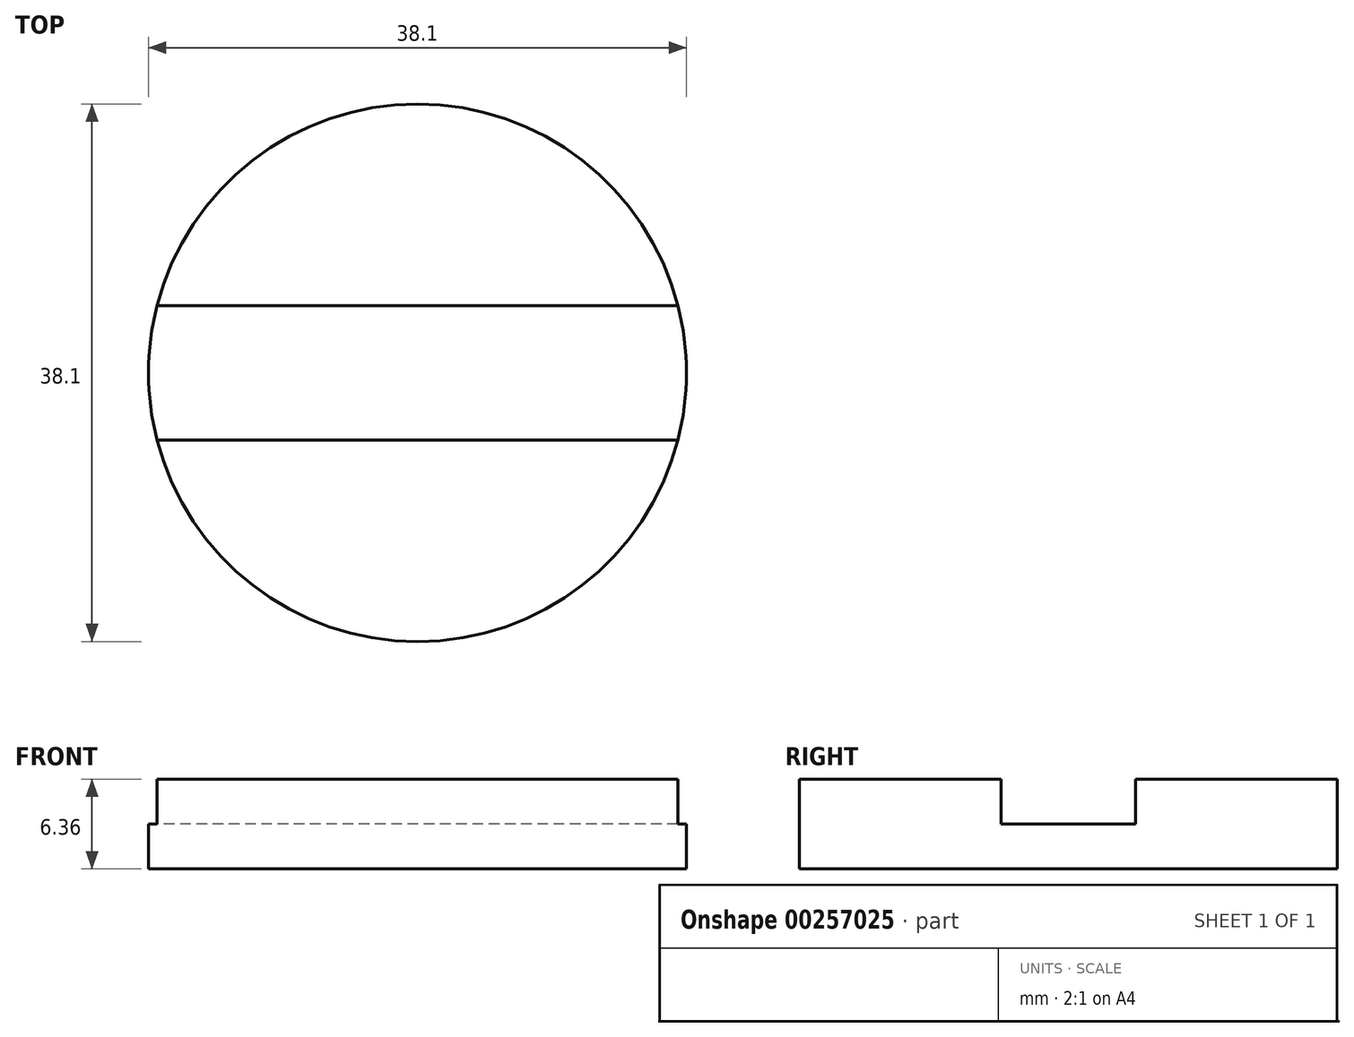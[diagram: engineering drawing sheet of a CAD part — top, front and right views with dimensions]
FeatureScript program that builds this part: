
annotation { "Feature Type Name" : "Feature", "Feature Type Description" : "" }
export const myFeature = defineFeature(function(context is Context, id is Id, definition is map)
    precondition{}
    {
        {
            var Q0;
            Q0=qCreatedBy(makeId("Top.planeOp"),FACE);
            var sketch = newSketch(context, id + "F0", { "sketchPlane" : qUnion([Q0])});
            skCircle(sketch, "E0", {"center": v(0, 0) * mm, "radius": 19.05 * mm});
            skLineSegment(sketch, "E1.bottom", {"start": v(18.45, 4.76) * mm, "end": v(-18.45, 4.76) * mm});
            skLineSegment(sketch, "E1.top", {"start": v(18.45, -4.76) * mm, "end": v(-18.45, -4.76) * mm});
            skLineSegment(sketch, "E1.left", {"start": v(18.45, 4.76) * mm, "end": v(18.45, -4.76) * mm});
            skLineSegment(sketch, "E1.right", {"start": v(-18.45, 4.76) * mm, "end": v(-18.45, -4.76) * mm});
            skLineSegment(sketch, "E2.bottom", {"start": v(25.4, 25.4) * mm, "end": v(-25.4, 25.4) * mm});
            skLineSegment(sketch, "E2.top", {"start": v(25.4, -25.4) * mm, "end": v(-25.4, -25.4) * mm});
            skLineSegment(sketch, "E2.left", {"start": v(25.4, 25.4) * mm, "end": v(25.4, -25.4) * mm});
            skLineSegment(sketch, "E2.right", {"start": v(-25.4, 25.4) * mm, "end": v(-25.4, -25.4) * mm});
            skLineSegment(sketch, "E3.bottom", {"start": v(-18.45, 4.76) * mm, "end": v(-25.4, 4.76) * mm});
            skLineSegment(sketch, "E3.top", {"start": v(-18.45, -4.76) * mm, "end": v(-25.4, -4.76) * mm});
            skLineSegment(sketch, "E3.right", {"start": v(-25.4, 4.76) * mm, "end": v(-25.4, -4.76) * mm});
            skLineSegment(sketch, "E4.bottom", {"start": v(-25.4, 4.76) * mm, "end": v(25.4, 4.76) * mm});
            skLineSegment(sketch, "E4.top", {"start": v(-25.4, -4.76) * mm, "end": v(25.4, -4.76) * mm});
            skLineSegment(sketch, "E4.right", {"start": v(25.4, 4.76) * mm, "end": v(25.4, -4.76) * mm});
            skSolve(sketch);
        }
        {
            var Q0;
            {var subQ0=sQuery(id+"F0.wireOp",EDGE,"E4.bottom");var subQ1=sQuery(id+"F0.wireOp",EDGE,"E0");var subQ2=makeQuery(id+"F0.imprint","INTERSECT",VERTEX,{"derivedFrom":[subQ1,sQuery(id+"F0.wireOp",EDGE,"E1.left"),subQ0]});Q0=makeQuery(id+"F0.imprint","IMPRINT",FACE,{"disambiguationData":[TD([[makeQuery(id+"F0.imprint","IMPRINT",EDGE,{"disambiguationData":[TD([[subQ2,-1.0]])],"derivedFrom":subQ1}),1.0]])]});}
            var Q1;
            {var subQ0=sQuery(id+"F0.wireOp",EDGE,"E4.top");var subQ1=sQuery(id+"F0.wireOp",EDGE,"E0");var subQ2=makeQuery(id+"F0.imprint","INTERSECT",VERTEX,{"derivedFrom":[subQ1,sQuery(id+"F0.wireOp",EDGE,"E1.left"),subQ0]});Q1=makeQuery(id+"F0.imprint","IMPRINT",FACE,{"disambiguationData":[TD([[makeQuery(id+"F0.imprint","IMPRINT",EDGE,{"disambiguationData":[TD([[subQ2,1.0]])],"derivedFrom":subQ1}),1.0]])]});}
            extrude(context, id + "F1", {"entities" : qUnion([Q0, Q1]), "depth" : 3.17 * mm});
        }
        {
            var Q0;
            {var subQ0=sQuery(id+"F0.wireOp",EDGE,"E4.bottom");var subQ1=sQuery(id+"F0.wireOp",EDGE,"E0");var subQ2=makeQuery(id+"F0.imprint","INTERSECT",VERTEX,{"derivedFrom":[subQ1,sQuery(id+"F0.wireOp",EDGE,"E1.left"),subQ0]});Q0=makeQuery(id+"F0.imprint","IMPRINT",FACE,{"disambiguationData":[TD([[makeQuery(id+"F0.imprint","IMPRINT",EDGE,{"disambiguationData":[TD([[subQ2,-1.0]])],"derivedFrom":subQ1}),1.0]])]});}
            var Q1;
            {var subQ0=sQuery(id+"F0.wireOp",EDGE,"E1.right");Q1=makeQuery(id+"F0.imprint","IMPRINT",FACE,{"disambiguationData":[TD([[makeQuery(id+"F0.imprint","IMPRINT",EDGE,{"derivedFrom":subQ0}),-1.0]])]});}
            var Q2;
            {var subQ0=sQuery(id+"F0.wireOp",EDGE,"E1.left");Q2=makeQuery(id+"F0.imprint","IMPRINT",FACE,{"disambiguationData":[TD([[makeQuery(id+"F0.imprint","IMPRINT",EDGE,{"derivedFrom":subQ0}),-1.0]])]});}
            var Q3;
            {var subQ0=sQuery(id+"F0.wireOp",EDGE,"E4.top");var subQ1=sQuery(id+"F0.wireOp",EDGE,"E0");var subQ2=makeQuery(id+"F0.imprint","INTERSECT",VERTEX,{"derivedFrom":[subQ1,sQuery(id+"F0.wireOp",EDGE,"E1.left"),subQ0]});Q3=makeQuery(id+"F0.imprint","IMPRINT",FACE,{"disambiguationData":[TD([[makeQuery(id+"F0.imprint","IMPRINT",EDGE,{"disambiguationData":[TD([[subQ2,1.0]])],"derivedFrom":subQ1}),1.0]])]});}
            var Q4;
            {var subQ0=sQuery(id+"F0.wireOp",EDGE,"E1.left");Q4=makeQuery(id+"F0.imprint","IMPRINT",FACE,{"disambiguationData":[TD([[makeQuery(id+"F0.imprint","IMPRINT",EDGE,{"derivedFrom":subQ0}),1.0]])]});}
            extrude(context, id + "F2", {"entities" : qUnion([Q0, Q1, Q2, Q3, Q4]), "operationType" : NewBodyOperationType.ADD, "oppositeDirection" : true, "depth" : 3.17 * mm});
        }
    });
